# Revit family: HL_Трап для внутренних помещений_HL70R
name_source: partatom
category: Instalační zařizovací předměty
revit_build: Autodesk Revit 2016 (Build: 20161004_0715(x64)
units: mm (PartAtom-declared; Revit-internal decimal feet)

## family parameters
Bod výpočtu místnosti = Ano
Kóta kulaté spojky = Použít průměr
Nadpis OmniClass = Deck Waste Water Drains
Ořezat dutým tvarem při načtení = Ne
Sdílené = Ano
Typ součásti = Normální
Vždy vertikální = Ano
Založené na pracovní rovině = Ne
Číslo OmniClass = 23.70.50.21.24.14

## types (1)
- HL_Трап для внутренних помещений_HL70R
    EAN = 9003076011971
    Klíčová poznámka = HL70R
    Komentáře k typům = Трап для внутренних помещений DN75/110 горизонтальный с предохранительным затвором обратного потока воды и тремя входными отверстиями DN40/50,с круглой насадкой d 131мм/d 112мм
    Model = HL70R
    Popis = Трап для внутренних помещений
    Připojení CW = Ne
    Připojení HW = Ne
    Připojení odpadu = Ano
    Připojení ventilace = Ne
    URL = http://www.hutterer-lechner.com
    Výrobce = HL Hutterer & Lechner GmbH
    ВЕС = 1,147 kg
    ВЫСОТА МОНТАЖА = 198 mm
    МАКСИМАЛЬНАЯ НАГРУЗКА КЛАССА = K3 - 300 kg
    МАТЕРИАЛ = PE
    НАСАДКА = 20-75mm / d 133mm / PP-V2A
    ПРИЁМНОЕ ОТВЕРСТИЕ = 3 x DN40/50
    ПРОИЗВОДИТЕЛЬНОСТЬ = 1,12 l/s
    РАЗМЕР = DN75/110
    РЕШЁТКА = d 112mm / V2A

## geometry (parser evidence)
native form markers: Sweep x35
no freeform markers — native parametric forms only
